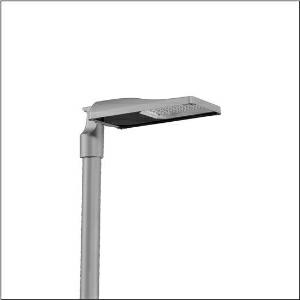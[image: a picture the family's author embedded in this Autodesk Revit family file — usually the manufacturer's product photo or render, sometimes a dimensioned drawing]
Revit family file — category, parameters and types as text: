
# Revit family: streetlight_sl_31_mini___st1_0a_5xh6d31b08ha_b8a3
name_source: partatom
category: Lighting Fixtures
units: mm (PartAtom-declared; Revit-internal decimal feet)

## family parameters
Cut with Voids When Loaded = No
Host = Face
Light Source = No
Part Type = Normal
Room Calculation Point = No
Round Connector Dimension = Use Diameter
Shared = No

## types (1)
- --- (1 x LED, 9240 lm, 68.3 W, 3000K)
    Apparent Load = 68 VA
    CIE Flux Codes = 37 72 97 100 100
    Color Rendering = 70
    Color Temperature = 3000K
    Default Elevation = 1800 mm
    Description = Streetlight SL 31 mini Easy, LST, Desk-Remote mast luminaire for post-top, side-entry; light control with lens of PMMA; light distribution: ST1.0a, direct asymmetric distribution, for standard-compliant lighting for roads and squares; LED: luminous flux: 9.240lm, light colour: 730, colour temperature: 3000K; luminous efficacy: 135,3lm/W; control: pre-setting: linear dimming characteristic, flexible luminous flux parameterisation, time-dependent luminous flux control, constant luminous flux control, power reduction, intelligent temperature release in ECG and LED module, overheat protection; luminaire housing, of diecast aluminium, Siteco® metallic grey (DB 702S), corrosivity category C5 high according to DIN EN ISO 12944; cover of toughened safety glass, transparent, opened without tools; mast flange of diecast aluminium, Siteco® metallic grey (DB 702S), spigot size: 76/60mm, mast flange included unmounted; with cable H07RN-F 3x 1.5mm², cable length: 8,5m, connection cable pre-assembled; mains connection: 220..240V, AC, 50/60Hz; power consumption (at start of service life): 68,3W / (at end of service life): 74,8W / (with reduced operation 50%): 29,7W; protection rating (complete): IP66; insulation class (complete): insulation class II (safety insulation); impact resistance: IK10; certification: CE, ENEC, ENEC+, VDE, UKCA; permissible operating ambient temperature for outdoor applications: -40..+50°C; packaging unit: 1 piece

Light Distribution: ST1.0a
    Height = 76 mm
    Lamp = 1 x LED
    Lamp Light Flux = 9240 lm
    Lamp Power = 68.3 W
    Lamp count = 1
    Length = 547 mm
    Luminous efficacy = 135 lm/W
    Manufacturer = Siteco
    ModVariant = No
    Model = 5XH6D31B08HA
    Number of Poles = 1
    OnlyDefault = Yes
    Power Factor = 1
    Product Name = Streetlight SL 31 mini | ST1.0a
    Product group = mast luminaire | pylon top
    ProductGroupID = 6100
    Protection Class = Protection class II
    Protection Degree = IP 66
    RLX_Detail_Level = 1
    RLX_Emergency_Light_Flux = 0 lm
    RLX_Emergency_Type = 0
    RLX_Emergency_Type_DB = No
    RlxData = <blob elided: 39441 chars, md5=d29bb19e>
    Socket = socket
    Standby Power = 0 W
    System Light Flux = 9240 lm
    System Power = 68 W
    Type Comments = factory setting: luminous flux: 100 % | dim-lin: 254 | 693 mA
    Type Image = l_1300326.jpg
    URL = http://relux.com
    VarID = @adj_054154
    Voltage = 0 V
    Weight = 0.00 kg
    Width = 265 mm

## geometry (parser evidence)
native form markers: Blend x4, Sweep x9
no freeform markers — native parametric forms only
